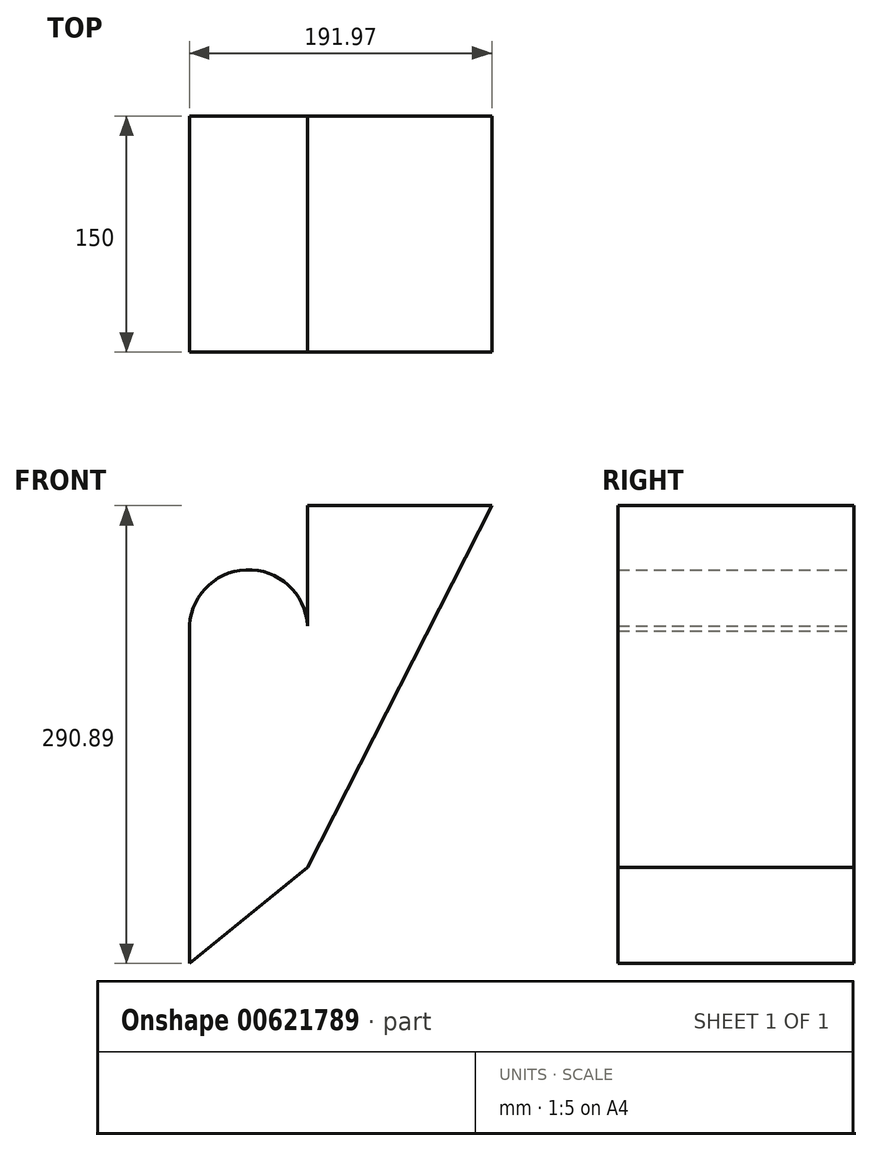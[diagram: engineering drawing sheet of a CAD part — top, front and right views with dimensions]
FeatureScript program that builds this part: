
annotation { "Feature Type Name" : "Feature", "Feature Type Description" : "" }
export const myFeature = defineFeature(function(context is Context, id is Id, definition is map)
    precondition{}
    {
        {
            var Q0;
            Q0=qCreatedBy(makeId("Front.planeOp"),FACE);
            var sketch = newSketch(context, id + "F0", { "sketchPlane" : qUnion([Q0])});
            skLineSegment(sketch, "E0", {"start": v(-74.94, 74.73) * mm, "end": v(-74.94, -95.97) * mm});
            skPoint(sketch, "E1.first.point", {"position": v(0, 73.9) * mm});
            skPoint(sketch, "E1.third.point", {"position": v(-28.58, 39.73) * mm});
            skLineSegment(sketch, "E2", {"start": v(0, 154.42) * mm, "end": v(0, 78.09) * mm});
            skLineSegment(sketch, "E3", {"start": v(117.03, 154.42) * mm, "end": v(0, 154.42) * mm});
            skLineSegment(sketch, "E4", {"start": v(-74.94, -95.97) * mm, "end": v(-74.94, -136.47) * mm});
            skLineSegment(sketch, "E5", {"start": v(-74.94, -136.47) * mm, "end": v(0, -75.23) * mm});
            skPoint(sketch, "E6.start.orphan", {"position": v(0, -47.92) * mm});
            skLineSegment(sketch, "E7", {"start": v(0, -75.23) * mm, "end": v(117.03, 154.42) * mm});
            skArc(sketch, "E8", {"start": v(0, 78.09) * mm, "mid": v(-39.13, 113.64) * mm, "end": v(-74.92, 74.73) * mm});
            skLineSegment(sketch, "E9", {"start": v(-74.94, 74.73) * mm, "end": v(-74.92, 74.73) * mm});
            skLineSegment(sketch, "E10.trimOffspring", {"start": v(0, 78.09) * mm, "end": v(0, 154.42) * mm});
            skSolve(sketch);
        }
        {
            var Q0;
            Q0=makeQuery(id+"F0.imprint","IMPRINT",FACE,{"disambiguationData":[TD([[makeQuery(id+"F0.imprint","IMPRINT",EDGE,{"derivedFrom":sQuery(id+"F0.wireOp",EDGE,"E0")}),1.0]])]});
            var Q1;
            Q1=sQuery(id+"F0.wireOp",EDGE,"E8");
            var Q2;
            Q2=sQuery(id+"F0.wireOp",EDGE,"E0");
            var Q3;
            Q3=sQuery(id+"F0.wireOp",EDGE,"E10.trimOffspring");
            var Q4;
            Q4=sQuery(id+"F0.wireOp",EDGE,"E7");
            var Q5;
            Q5=sQuery(id+"F0.wireOp",EDGE,"E5");
            var Q6;
            Q6=sQuery(id+"F0.wireOp",EDGE,"E4");
            extrude(context, id + "F1", {"entities" : qUnion([Q0]), "surfaceEntities" : qUnion([Q1, Q2, Q3, Q4, Q5, Q6]), "endBound" : BoundingType.SYMMETRIC, "depth" : 150 * mm, "offsetDistance" : 25 * mm});
        }
    });
